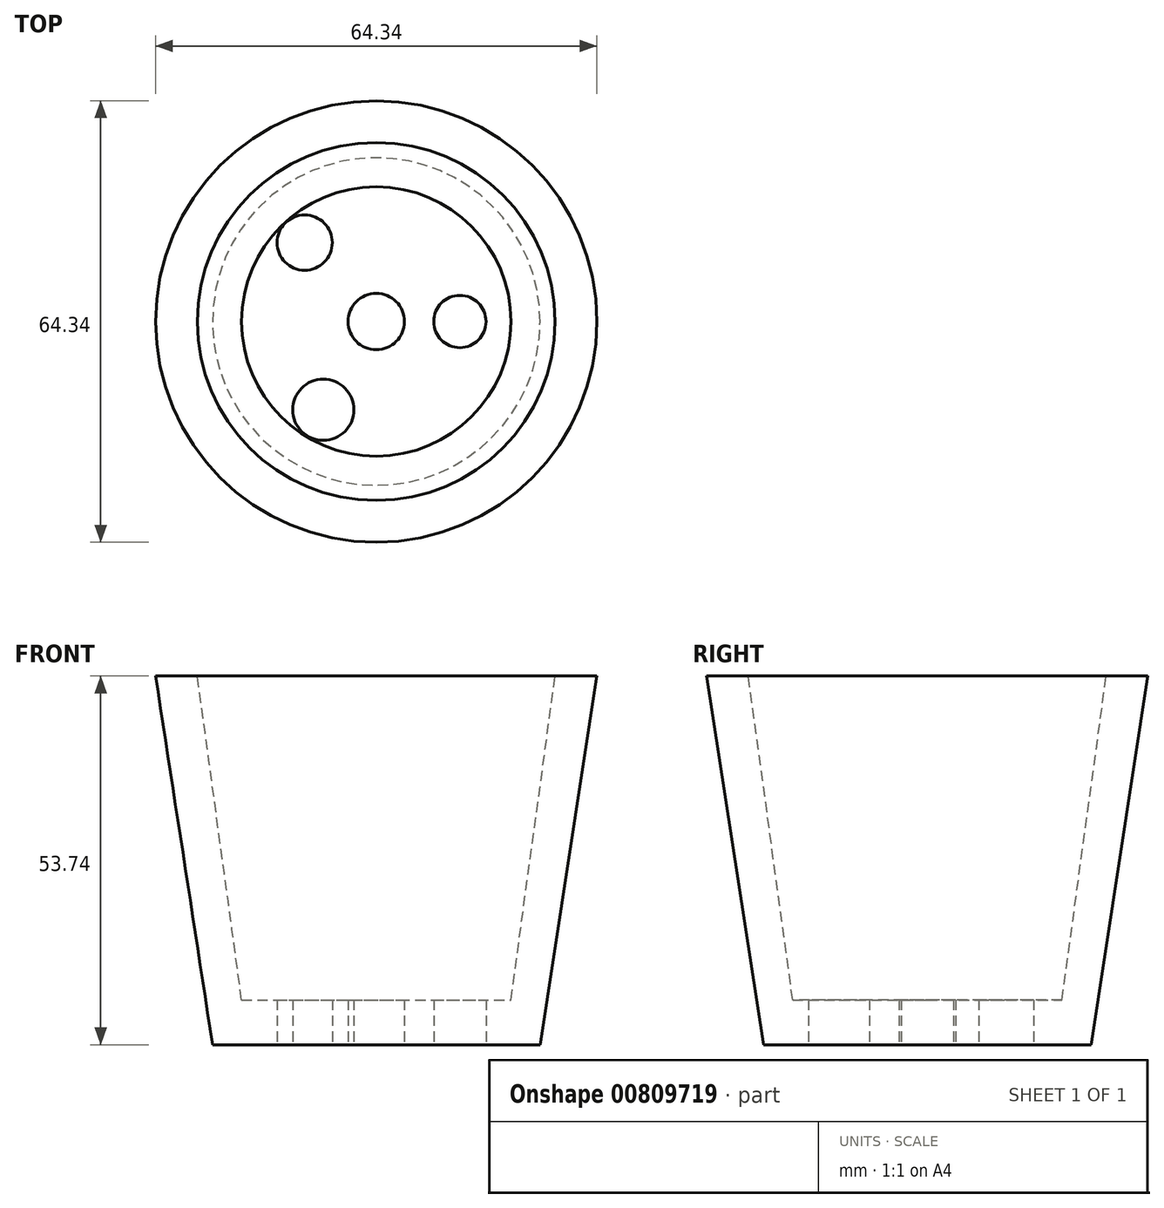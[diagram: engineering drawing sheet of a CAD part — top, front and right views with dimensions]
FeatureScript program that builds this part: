
annotation { "Feature Type Name" : "Feature", "Feature Type Description" : "" }
export const myFeature = defineFeature(function(context is Context, id is Id, definition is map)
    precondition{}
    {
        {
            var Q0;
            Q0=qCreatedBy(makeId("Front.planeOp"),FACE);
            var sketch = newSketch(context, id + "F0", { "sketchPlane" : qUnion([Q0])});
            skLineSegment(sketch, "E0", {"start": v(0, 6.54) * mm, "end": v(-19.63, 6.54) * mm});
            skLineSegment(sketch, "E1", {"start": v(-19.63, 6.54) * mm, "end": v(-26.09, 53.74) * mm});
            skLineSegment(sketch, "E2", {"start": v(-26.09, 53.74) * mm, "end": v(-32.17, 53.74) * mm});
            skLineSegment(sketch, "E3", {"start": v(-32.17, 53.74) * mm, "end": v(-23.87, 0) * mm});
            skLineSegment(sketch, "E4", {"start": v(-23.87, 0) * mm, "end": v(0, 0) * mm});
            skLineSegment(sketch, "E5", {"start": v(0, 0) * mm, "end": v(0, 6.54) * mm});
            skSolve(sketch);
        }
        {
            var Q0;
            Q0=makeQuery(id+"F0.imprint","IMPRINT",FACE,{"disambiguationData":[TD([[makeQuery(id+"F0.imprint","IMPRINT",EDGE,{"derivedFrom":sQuery(id+"F0.wireOp",EDGE,"E0")}),1.0]])]});
            var Q1;
            Q1=sQuery(id+"F0.wireOp",EDGE,"E5");
            revolve(context, id + "F1", {"surfaceOperationType" : NewSurfaceOperationType.NEW, "entities" : qUnion([Q0]), "axis" : qUnion([Q1]), "revolveType" : RevolveType.FULL});
        }
        {
            var Q0;
            Q0=makeQuery(id+"F1.opRevolve","SWEPT_FACE",FACE,{"disambiguationData":[OSD([sQuery(id+"F0.wireOp",EDGE,"E4")])]});
            var sketch = newSketch(context, id + "F2", { "sketchPlane" : qUnion([Q0])});
            skCircle(sketch, "E6", {"center": v(0, 0) * mm, "radius": 4.11 * mm});
            skCircle(sketch, "E7", {"center": v(-7.72, 12.86) * mm, "radius": 4.46 * mm});
            skCircle(sketch, "E8", {"center": v(12.2, 0) * mm, "radius": 3.81 * mm});
            skCircle(sketch, "E9", {"center": v(-10.44, -11.5) * mm, "radius": 4.03 * mm});
            skSolve(sketch);
        }
        {
            var Q0;
            Q0 = qSketchRegion(id + "F2", true);
            extrude(context, id + "F3", {"entities" : qUnion([Q0]), "operationType" : NewBodyOperationType.REMOVE, "oppositeDirection" : true, "depth" : 25.4 * mm, "offsetDistance" : 25.4 * mm});
        }
    });
